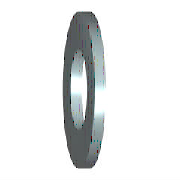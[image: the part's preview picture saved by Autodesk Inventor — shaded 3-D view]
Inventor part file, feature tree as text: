
AUTODESK INVENTOR PART (.ipt)
format: ipt  version: 2022 (Build 260153000, 153)  size: 107,520 bytes
history: native  units: mm (DEFAULTED — no unit token found)
features: extrude x1, other x1, plane x1, sketch x1
ambient origin geometry x7: Origin, YZ Plane, XY Plane, X Axis, Y Axis, Z Axis, Center Point
bodies: Solid1 (feature_tree)
feature tree (4):
  extrude  "Базовый элемент"  Depth=3.2mm
  other  "Work Axis1"
  plane  "Work Plane1"
  sketch  "Эскиз"
